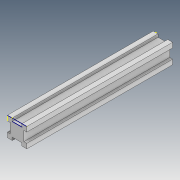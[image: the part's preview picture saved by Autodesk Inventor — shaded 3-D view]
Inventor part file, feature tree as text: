
AUTODESK INVENTOR PART (.ipt)
format: ipt  version: 2021 (Build 250183000, 183)  size: 119,296 bytes
history: native  units: mm
features: sketch x4, other x1, extrude x1
ambient origin geometry x8: Origin, YZ Plane, XZ Plane, XY Plane, X Axis, Y Axis, Z Axis, Center Point
bodies: Body1 (feature_tree)
feature tree (6):
  other  "Sólido1"
  extrude  "Extrusão1"  Depth=5.0mm
  sketch  "Esboço2"  dims[d6=3.0mm]
  sketch  "Esboço3"  dims[d7=10.0mm]
  sketch  "Esboço4"  dims[d8=3.0mm d9=5.0mm d10=5.0mm d11=3.0mm d12=10.0mm d13=5.0mm d14=5.0mm d15=3.0mm d16=10.0mm d17=3.0mm d18=5.0mm d19=3.0mm d20=10.0mm d21=150.0mm d22=0.0mm]
  sketch  "Esboço1"  dims[d4=5.0mm d5=5.0mm]
